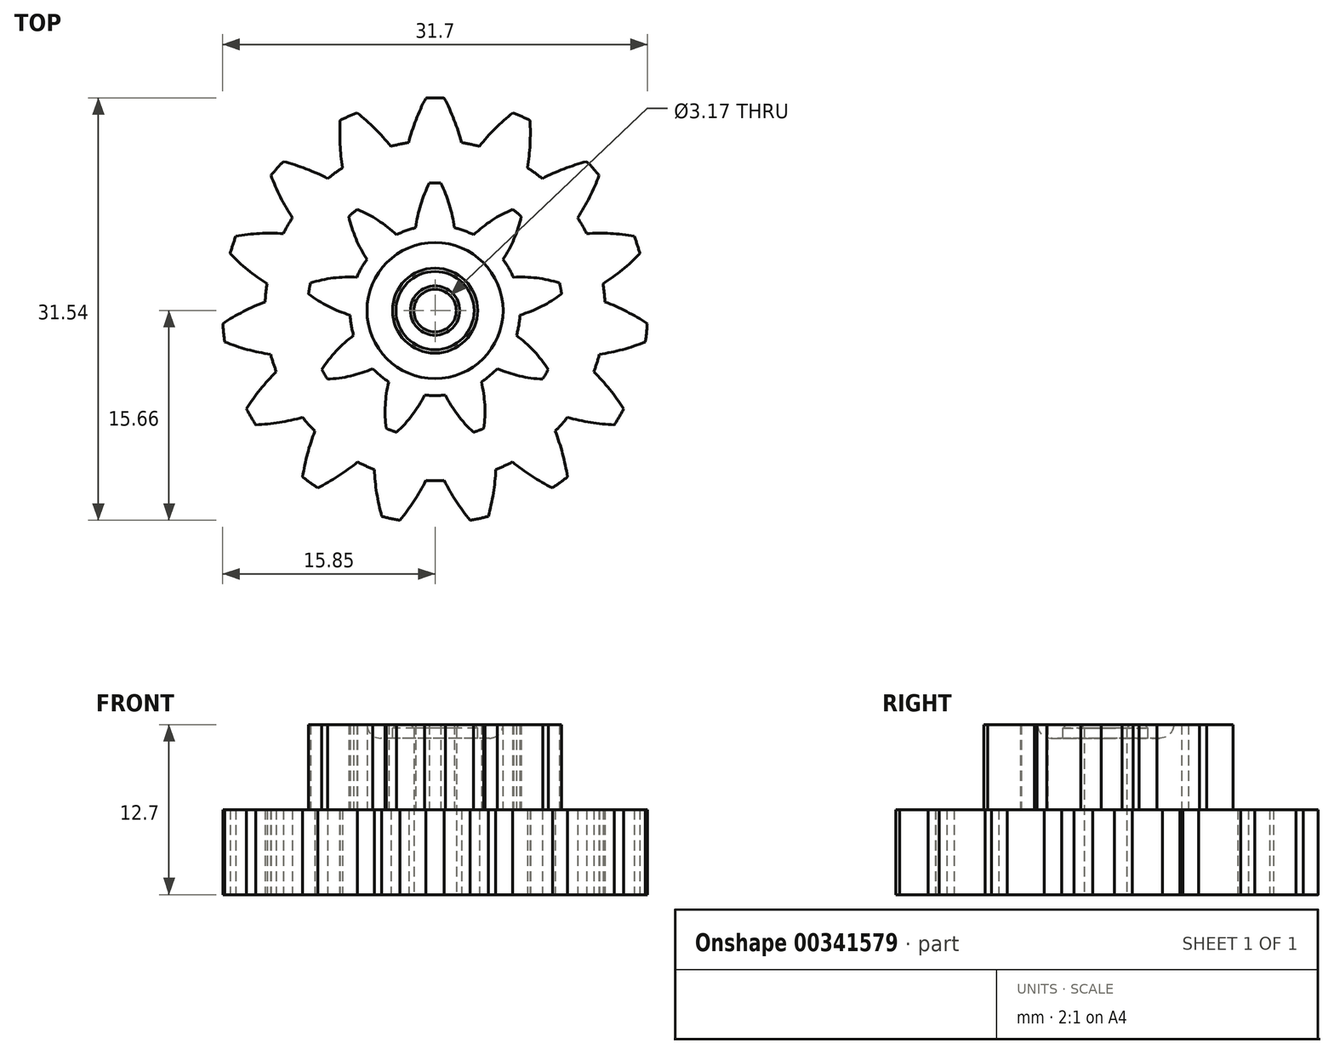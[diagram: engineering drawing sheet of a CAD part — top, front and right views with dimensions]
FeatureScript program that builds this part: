
annotation { "Feature Type Name" : "Feature", "Feature Type Description" : "" }
export const myFeature = defineFeature(function(context is Context, id is Id, definition is map)
    precondition{}
    {
        {
            var Q0;
            Q0=qCreatedBy(makeId("Top.planeOp"),FACE);
            var sketch = newSketch(context, id + "F0", { "sketchPlane" : qUnion([Q0])});
            skCircle(sketch, "E0", {"center": v(0, 0) * mm, "radius": 12.7 * mm});
            skCircle(sketch, "E1", {"center": v(0, 0) * mm, "radius": 15.88 * mm, "construction": true});
            skLineSegment(sketch, "E2", {"start": v(0, 0) * mm, "end": v(-19.6, 12.5) * mm, "construction": true});
            skLineSegment(sketch, "E3", {"start": v(0, 0) * mm, "end": v(20.1, 12.8) * mm, "construction": true});
            skCircle(sketch, "E4", {"center": v(-13.39, 8.53) * mm, "radius": 15.88 * mm, "construction": true});
            skCircle(sketch, "E5", {"center": v(13.39, 8.53) * mm, "radius": 15.88 * mm, "construction": true});
            skArc(sketch, "E6", {"start": v(-1.97, 12.55) * mm, "mid": v(-1.42, 14.24) * mm, "end": v(-0.7, 15.86) * mm});
            skArc(sketch, "E7", {"start": v(1.97, 12.55) * mm, "mid": v(1.42, 14.24) * mm, "end": v(0.7, 15.86) * mm});
            skArc(sketch, "E8", {"start": v(-0.7, 15.86) * mm, "mid": v(0, 15.87) * mm, "end": v(0.7, 15.86) * mm});
            skCircle(sketch, "E9", {"center": v(0, 0) * mm, "radius": 1.59 * mm});
            skCircle(sketch, "E10", {"center": v(0, 0) * mm, "radius": 4.76 * mm});
            skSolve(sketch);
        }
        {
            var Q0;
            Q0 = qSketchRegion(id + "F0", true);
            var Q1;
            Q1=makeQuery(id+"F0.imprint","IMPRINT",FACE,{"disambiguationData":[TD([[makeQuery(id+"F0.imprint","IMPRINT",EDGE,{"derivedFrom":sQuery(id+"F0.wireOp",EDGE,"E9")}),-1.0]])]});
            extrude(context, id + "F1", {"entities" : qUnion([Q0, Q1]), "depth" : 6.35 * mm});
        }
        {
            var Q0;
            Q0=makeQuery(id+"F1.opExtrude","SWEPT_BODY",BODY,{"disambiguationData":[OSD([sQuery(id+"F0.wireOp",EDGE,"E0"),sQuery(id+"F0.wireOp",EDGE,"E6"),sQuery(id+"F0.wireOp",EDGE,"E7"),sQuery(id+"F0.wireOp",EDGE,"E8"),sQuery(id+"F0.wireOp",EDGE,"E9")])]});
            var Q1;
            Q1=makeQuery(id+"F1.opExtrude","SWEPT_FACE",FACE,{"disambiguationData":[OSD([sQuery(id+"F0.wireOp",EDGE,"E0")])]});
            circularPattern(context, id + "F2", {"operationType" : NewBodyOperationType.ADD, "entities" : qUnion([Q0]), "axis" : qUnion([Q1]), "angle" : 360 * degree, "instanceCount" : 15, "equalSpace" : true});
        }
        {
            var Q0;
            {var subQ0=makeQuery(id+"F1.opExtrude","CAP_FACE",FACE,{"disambiguationData":[OSD([sQuery(id+"F0.wireOp",EDGE,"E0"),sQuery(id+"F0.wireOp",EDGE,"E6"),sQuery(id+"F0.wireOp",EDGE,"E7"),sQuery(id+"F0.wireOp",EDGE,"E8"),sQuery(id+"F0.wireOp",EDGE,"E9")])],"isStart":false});Q0=makeQuery(id+"F2.boolean.opBoolean","MERGE",FACE,{"derivedFrom":[subQ0,makeQuery(id+"F2.opPattern","COPY",FACE,{"derivedFrom":subQ0,"instanceName":"1"}),makeQuery(id+"F2.opPattern","COPY",FACE,{"derivedFrom":subQ0,"instanceName":"2"}),makeQuery(id+"F2.opPattern","COPY",FACE,{"derivedFrom":subQ0,"instanceName":"3"}),makeQuery(id+"F2.opPattern","COPY",FACE,{"derivedFrom":subQ0,"instanceName":"4"}),makeQuery(id+"F2.opPattern","COPY",FACE,{"derivedFrom":subQ0,"instanceName":"5"}),makeQuery(id+"F2.opPattern","COPY",FACE,{"derivedFrom":subQ0,"instanceName":"6"}),makeQuery(id+"F2.opPattern","COPY",FACE,{"derivedFrom":subQ0,"instanceName":"7"}),makeQuery(id+"F2.opPattern","COPY",FACE,{"derivedFrom":subQ0,"instanceName":"8"}),makeQuery(id+"F2.opPattern","COPY",FACE,{"derivedFrom":subQ0,"instanceName":"9"}),makeQuery(id+"F2.opPattern","COPY",FACE,{"derivedFrom":subQ0,"instanceName":"10"}),makeQuery(id+"F2.opPattern","COPY",FACE,{"derivedFrom":subQ0,"instanceName":"11"}),makeQuery(id+"F2.opPattern","COPY",FACE,{"derivedFrom":subQ0,"instanceName":"12"})]});}
            var sketch = newSketch(context, id + "F3", { "sketchPlane" : qUnion([Q0])});
            skCircle(sketch, "E11", {"center": v(0, 0) * mm, "radius": 6.35 * mm});
            skCircle(sketch, "E12", {"center": v(0, 0) * mm, "radius": 1.59 * mm});
            skCircle(sketch, "E13", {"center": v(0, 0) * mm, "radius": 9.53 * mm, "construction": true});
            skLineSegment(sketch, "E14", {"start": v(0, 0) * mm, "end": v(-6.82, 4.35) * mm, "construction": true});
            skLineSegment(sketch, "E15", {"start": v(0, 0) * mm, "end": v(8.03, 5.12) * mm, "construction": true});
            skArc(sketch, "E16", {"start": v(1.43, 6.19) * mm, "mid": v(1.08, 7.9) * mm, "end": v(0.42, 9.52) * mm});
            skArc(sketch, "E17", {"start": v(-1.43, 6.19) * mm, "mid": v(-1.08, 7.9) * mm, "end": v(-0.42, 9.52) * mm});
            skArc(sketch, "E18", {"start": v(-0.42, 9.52) * mm, "mid": v(0.06, 9.52) * mm, "end": v(0.53, 9.51) * mm});
            skArc(sketch, "E19.1.0", {"start": v(-2.88, 5.66) * mm, "mid": v(-4.25, 6.74) * mm, "end": v(-5.8, 7.56) * mm});
            skArc(sketch, "E19.1.1", {"start": v(-6.43, 7.02) * mm, "mid": v(-6.08, 7.33) * mm, "end": v(-5.71, 7.62) * mm});
            skArc(sketch, "E19.1.2", {"start": v(-5.07, 3.82) * mm, "mid": v(-5.9, 5.36) * mm, "end": v(-6.43, 7.02) * mm});
            skArc(sketch, "E19.2.0", {"start": v(-5.84, 2.48) * mm, "mid": v(-7.6, 2.43) * mm, "end": v(-9.3, 2.06) * mm});
            skArc(sketch, "E19.2.1", {"start": v(-9.44, 1.24) * mm, "mid": v(-9.37, 1.7) * mm, "end": v(-9.27, 2.17) * mm});
            skArc(sketch, "E19.2.2", {"start": v(-6.34, -0.34) * mm, "mid": v(-7.97, 0.31) * mm, "end": v(-9.44, 1.24) * mm});
            skArc(sketch, "E19.3.0", {"start": v(-6.07, -1.85) * mm, "mid": v(-7.38, -3.02) * mm, "end": v(-8.45, -4.4) * mm});
            skArc(sketch, "E19.3.1", {"start": v(-8.03, -5.12) * mm, "mid": v(-8.28, -4.71) * mm, "end": v(-8.5, -4.3) * mm});
            skArc(sketch, "E19.3.2", {"start": v(-4.64, -4.33) * mm, "mid": v(-6.3, -4.88) * mm, "end": v(-8.03, -5.12) * mm});
            skArc(sketch, "E19.4.0", {"start": v(-3.46, -5.32) * mm, "mid": v(-3.71, -7.05) * mm, "end": v(-3.65, -8.8) * mm});
            skArc(sketch, "E19.4.1", {"start": v(-2.86, -9.08) * mm, "mid": v(-3.3, -8.93) * mm, "end": v(-3.75, -8.76) * mm});
            skArc(sketch, "E19.4.2", {"start": v(-0.77, -6.3) * mm, "mid": v(-1.69, -7.8) * mm, "end": v(-2.86, -9.08) * mm});
            skArc(sketch, "E19.5.0", {"start": v(0.77, -6.3) * mm, "mid": v(1.69, -7.8) * mm, "end": v(2.86, -9.08) * mm});
            skArc(sketch, "E19.5.1", {"start": v(3.65, -8.8) * mm, "mid": v(3.2, -8.97) * mm, "end": v(2.76, -9.12) * mm});
            skArc(sketch, "E19.5.2", {"start": v(3.46, -5.32) * mm, "mid": v(3.71, -7.05) * mm, "end": v(3.65, -8.8) * mm});
            skArc(sketch, "E19.6.0", {"start": v(4.64, -4.33) * mm, "mid": v(6.3, -4.88) * mm, "end": v(8.03, -5.12) * mm});
            skArc(sketch, "E19.6.1", {"start": v(8.45, -4.4) * mm, "mid": v(8.22, -4.81) * mm, "end": v(7.97, -5.21) * mm});
            skArc(sketch, "E19.6.2", {"start": v(6.07, -1.85) * mm, "mid": v(7.38, -3.02) * mm, "end": v(8.45, -4.4) * mm});
            skArc(sketch, "E19.7.0", {"start": v(6.34, -0.34) * mm, "mid": v(7.97, 0.31) * mm, "end": v(9.44, 1.24) * mm});
            skArc(sketch, "E19.7.1", {"start": v(9.3, 2.06) * mm, "mid": v(9.39, 1.6) * mm, "end": v(9.46, 1.13) * mm});
            skArc(sketch, "E19.7.2", {"start": v(5.84, 2.48) * mm, "mid": v(7.6, 2.43) * mm, "end": v(9.3, 2.06) * mm});
            skCircle(sketch, "E20", {"center": v(0, 0) * mm, "radius": 3.18 * mm});
            skCircle(sketch, "E21", {"center": v(0, 0) * mm, "radius": 4.76 * mm});
            skCircle(sketch, "E22", {"center": v(-8.03, 5.12) * mm, "radius": 9.53 * mm, "construction": true});
            skCircle(sketch, "E23", {"center": v(8.03, 5.12) * mm, "radius": 9.53 * mm, "construction": true});
            skArc(sketch, "E24.1.8.0", {"start": v(5.07, 3.82) * mm, "mid": v(5.9, 5.36) * mm, "end": v(6.43, 7.02) * mm});
            skArc(sketch, "E24.4.8.0", {"start": v(5.8, 7.56) * mm, "mid": v(6.16, 7.26) * mm, "end": v(6.52, 6.95) * mm});
            skArc(sketch, "E24.8.8.0", {"start": v(2.88, 5.66) * mm, "mid": v(4.25, 6.74) * mm, "end": v(5.8, 7.56) * mm});
            skSolve(sketch);
        }
        {
            var Q0;
            Q0 = qSketchRegion(id + "F3", true);
            var Q1;
            Q1=makeQuery(id+"F3.imprint","IMPRINT",FACE,{"disambiguationData":[TD([[makeQuery(id+"F3.imprint","IMPRINT",EDGE,{"derivedFrom":sQuery(id+"F3.wireOp",EDGE,"E20")}),-1.0]])]});
            var Q2;
            Q2=makeQuery(id+"F3.imprint","IMPRINT",FACE,{"disambiguationData":[TD([[makeQuery(id+"F3.imprint","IMPRINT",EDGE,{"derivedFrom":sQuery(id+"F3.wireOp",EDGE,"E12")}),-1.0]])]});
            extrude(context, id + "F4", {"entities" : qUnion([Q0, Q1, Q2]), "operationType" : NewBodyOperationType.ADD, "depth" : 6.35 * mm});
        }
        {
            var Q0;
            Q0=makeQuery(id+"F4.opExtrude","CAP_FACE",FACE,{"disambiguationData":[OSD([sQuery(id+"F3.wireOp",EDGE,"E11"),sQuery(id+"F3.wireOp",EDGE,"E12"),sQuery(id+"F3.wireOp",EDGE,"E16"),sQuery(id+"F3.wireOp",EDGE,"E17"),sQuery(id+"F3.wireOp",EDGE,"E18"),sQuery(id+"F3.wireOp",EDGE,"E19.1.0"),sQuery(id+"F3.wireOp",EDGE,"E19.1.1"),sQuery(id+"F3.wireOp",EDGE,"E19.1.2"),sQuery(id+"F3.wireOp",EDGE,"E19.2.0"),sQuery(id+"F3.wireOp",EDGE,"E19.2.1"),sQuery(id+"F3.wireOp",EDGE,"E19.2.2"),sQuery(id+"F3.wireOp",EDGE,"E19.3.0"),sQuery(id+"F3.wireOp",EDGE,"E19.3.1"),sQuery(id+"F3.wireOp",EDGE,"E19.3.2"),sQuery(id+"F3.wireOp",EDGE,"E19.4.0"),sQuery(id+"F3.wireOp",EDGE,"E19.4.1"),sQuery(id+"F3.wireOp",EDGE,"E19.4.2"),sQuery(id+"F3.wireOp",EDGE,"E19.5.0"),sQuery(id+"F3.wireOp",EDGE,"E19.5.1"),sQuery(id+"F3.wireOp",EDGE,"E19.5.2"),sQuery(id+"F3.wireOp",EDGE,"E19.6.0"),sQuery(id+"F3.wireOp",EDGE,"E19.6.1"),sQuery(id+"F3.wireOp",EDGE,"E19.6.2"),sQuery(id+"F3.wireOp",EDGE,"E19.7.0"),sQuery(id+"F3.wireOp",EDGE,"E19.7.1"),sQuery(id+"F3.wireOp",EDGE,"E19.7.2"),sQuery(id+"F3.wireOp",EDGE,"E24.1.8.0"),sQuery(id+"F3.wireOp",EDGE,"E24.4.8.0"),sQuery(id+"F3.wireOp",EDGE,"E24.8.8.0")])],"isStart":false});
            var sketch = newSketch(context, id + "F5", { "sketchPlane" : qUnion([Q0])});
            skCircle(sketch, "E25", {"center": v(0, 0) * mm, "radius": 5.08 * mm});
            skCircle(sketch, "E26", {"center": v(0, 0) * mm, "radius": 3.18 * mm});
            skSolve(sketch);
        }
        {
            var Q0;
            Q0 = qSketchRegion(id + "F5", true);
            extrude(context, id + "F6", {"entities" : qUnion([Q0]), "operationType" : NewBodyOperationType.REMOVE, "oppositeDirection" : true, "depth" : 1.02 * mm});
        }
        {
            var Q0;
            Q0=makeQuery(id+"F6.boolean.opBoolean","COPY",EDGE,{"derivedFrom":makeQuery(id+"F6.opExtrude","CAP_EDGE",EDGE,{"disambiguationData":[OSD([sQuery(id+"F5.wireOp",EDGE,"E25")])],"isStart":false})});
            fillet(context, id + "F7", {"entities" : qUnion([Q0]), "radius" : 1.02 * mm, "tangentPropagation" : true, "allowEdgeOverflow" : false});
        }
        {
            var Q0;
            Q0=makeQuery(id+"F4.opExtrude","CAP_EDGE",EDGE,{"disambiguationData":[OSD([sQuery(id+"F3.wireOp",EDGE,"E12")])],"isStart":false});
            var Q1;
            Q1=makeQuery(id+"F6.boolean.opBoolean","COPY",EDGE,{"derivedFrom":makeQuery(id+"F6.opExtrude","CAP_EDGE",EDGE,{"disambiguationData":[OSD([sQuery(id+"F5.wireOp",EDGE,"E26")])],"isStart":true})});
            chamfer(context, id + "F8", {"entities" : qUnion([Q0, Q1]), "width" : 0.25 * mm, "tangentPropagation" : true});
        }
    });
